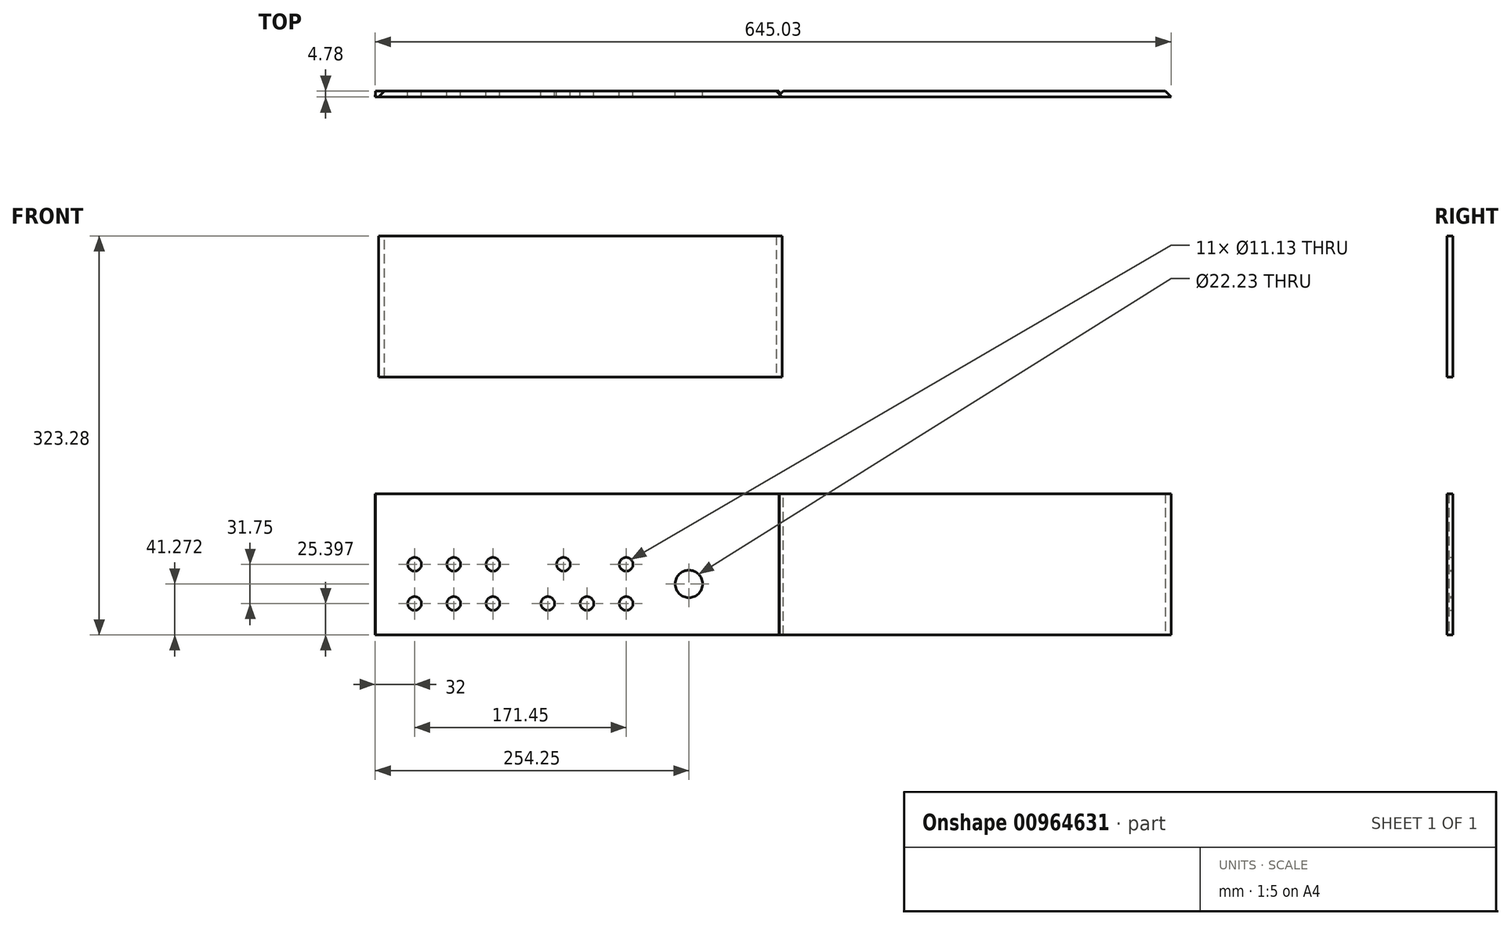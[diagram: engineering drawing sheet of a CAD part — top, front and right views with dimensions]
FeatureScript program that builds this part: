
annotation { "Feature Type Name" : "Feature", "Feature Type Description" : "" }
export const myFeature = defineFeature(function(context is Context, id is Id, definition is map)
    precondition{}
    {
        {
            var Q0;
            Q0=qCreatedBy(makeId("Front.planeOp"),FACE);
            var sketch = newSketch(context, id + "F0", { "sketchPlane" : qUnion([Q0])});
            skLineSegment(sketch, "E0.bottom", {"start": v(-189.37, 59.29) * mm, "end": v(137.66, 59.29) * mm});
            skLineSegment(sketch, "E0.top", {"start": v(-189.37, -55.01) * mm, "end": v(137.66, -55.01) * mm});
            skLineSegment(sketch, "E0.left", {"start": v(-189.37, 59.29) * mm, "end": v(-189.37, -55.01) * mm});
            skLineSegment(sketch, "E0.right", {"start": v(137.66, 59.29) * mm, "end": v(137.66, -55.01) * mm});
            skLineSegment(sketch, "E1.bottom", {"start": v(137.9, 59.29) * mm, "end": v(455.4, 59.29) * mm});
            skLineSegment(sketch, "E1.top", {"start": v(137.9, -55.01) * mm, "end": v(455.4, -55.01) * mm});
            skLineSegment(sketch, "E1.left", {"start": v(137.9, 59.29) * mm, "end": v(137.9, -55.01) * mm});
            skLineSegment(sketch, "E1.right", {"start": v(455.4, 59.29) * mm, "end": v(455.4, -55.01) * mm});
            skLineSegment(sketch, "E2.left", {"start": v(-189.62, 59.29) * mm, "end": v(-189.62, -55.01) * mm});
            skCircle(sketch, "E3", {"center": v(-157.62, -29.61) * mm, "radius": 5.56 * mm});
            skCircle(sketch, "E4", {"center": v(-125.87, -29.61) * mm, "radius": 5.56 * mm});
            skCircle(sketch, "E5", {"center": v(-94.12, -29.61) * mm, "radius": 5.56 * mm});
            skCircle(sketch, "E6", {"center": v(-17.92, -29.61) * mm, "radius": 5.56 * mm});
            skCircle(sketch, "E7", {"center": v(-49.67, -29.61) * mm, "radius": 5.56 * mm});
            skCircle(sketch, "E8", {"center": v(13.83, -29.61) * mm, "radius": 5.56 * mm});
            skCircle(sketch, "E9", {"center": v(-157.62, 2.14) * mm, "radius": 5.56 * mm});
            skCircle(sketch, "E10", {"center": v(-125.87, 2.14) * mm, "radius": 5.56 * mm});
            skCircle(sketch, "E11", {"center": v(-94.12, 2.14) * mm, "radius": 5.56 * mm});
            skCircle(sketch, "E12", {"center": v(-36.97, 2.14) * mm, "radius": 5.56 * mm});
            skCircle(sketch, "E13", {"center": v(13.83, 2.14) * mm, "radius": 5.56 * mm});
            skPoint(sketch, "E14", {"position": v(-157.62, -3.51) * mm});
            skCircle(sketch, "E15", {"center": v(64.63, -13.74) * mm, "radius": 11.11 * mm});
            skLineSegment(sketch, "E16", {"start": v(30.11, 2.14) * mm, "end": v(-174.63, 2.14) * mm, "construction": true});
            skLineSegment(sketch, "E17", {"start": v(-175, -29.61) * mm, "end": v(32.3, -29.61) * mm, "construction": true});
            skLineSegment(sketch, "E18", {"start": v(35.92, -13.74) * mm, "end": v(93.64, -13.74) * mm, "construction": true});
            skLineSegment(sketch, "E19.bottom", {"start": v(137.66, 59.29) * mm, "end": v(137.9, 59.29) * mm});
            skLineSegment(sketch, "E19.top", {"start": v(137.66, -55.01) * mm, "end": v(137.9, -55.01) * mm});
            skLineSegment(sketch, "E20.bottom", {"start": v(-189.62, 59.29) * mm, "end": v(-189.37, 59.29) * mm});
            skLineSegment(sketch, "E20.top", {"start": v(-189.62, -55.01) * mm, "end": v(-189.37, -55.01) * mm});
            skLineSegment(sketch, "E21.bottom", {"start": v(-186.96, 268.27) * mm, "end": v(140.07, 268.27) * mm});
            skLineSegment(sketch, "E21.top", {"start": v(-186.96, 153.97) * mm, "end": v(140.07, 153.97) * mm});
            skLineSegment(sketch, "E21.left", {"start": v(-186.96, 268.27) * mm, "end": v(-186.96, 153.97) * mm});
            skLineSegment(sketch, "E21.right", {"start": v(140.07, 268.27) * mm, "end": v(140.07, 153.97) * mm});
            skLineSegment(sketch, "E22.bottom", {"start": v(-507.12, 59.29) * mm, "end": v(-189.62, 59.29) * mm});
            skLineSegment(sketch, "E22.top", {"start": v(-507.12, -55.01) * mm, "end": v(-189.62, -55.01) * mm});
            skLineSegment(sketch, "E22.left", {"start": v(-507.12, 59.29) * mm, "end": v(-507.12, -55.01) * mm});
            skSolve(sketch);
        }
        {
            var Q0;
            Q0=makeQuery(id+"F0.imprint","IMPRINT",FACE,{"disambiguationData":[TD([[makeQuery(id+"F0.imprint","IMPRINT",EDGE,{"derivedFrom":sQuery(id+"F0.wireOp",EDGE,"E2.bottom")}),1.0]])]});
            var Q1;
            Q1=makeQuery(id+"F0.imprint","IMPRINT",FACE,{"disambiguationData":[TD([[makeQuery(id+"F0.imprint","IMPRINT",EDGE,{"derivedFrom":sQuery(id+"F0.wireOp",EDGE,"E0.bottom")}),-1.0]])]});
            var Q2;
            Q2=makeQuery(id+"F0.imprint","IMPRINT",FACE,{"disambiguationData":[TD([[makeQuery(id+"F0.imprint","IMPRINT",EDGE,{"derivedFrom":sQuery(id+"F0.wireOp",EDGE,"E1.bottom")}),-1.0]])]});
            extrude(context, id + "F1", {"entities" : qUnion([Q0, Q1, Q2]), "depth" : 4.78 * mm, "offsetDistance" : 25.4 * mm});
        }
        {
            var Q0;
            Q0=makeQuery(id+"F0.imprint","IMPRINT",FACE,{"disambiguationData":[TD([[makeQuery(id+"F0.imprint","IMPRINT",EDGE,{"derivedFrom":sQuery(id+"F0.wireOp",EDGE,"E20.bottom")}),-1.0]])]});
            var Q1;
            Q1=makeQuery(id+"F0.imprint","IMPRINT",FACE,{"disambiguationData":[TD([[makeQuery(id+"F0.imprint","IMPRINT",EDGE,{"derivedFrom":sQuery(id+"F0.wireOp",EDGE,"E19.bottom")}),-1.0]])]});
            extrude(context, id + "F2", {"entities" : qUnion([Q0, Q1]), "depth" : 1.59 * mm, "offsetDistance" : 25.4 * mm});
        }
        {
            var Q0;
            Q0=makeQuery(id+"F1.opExtrude","CAP_EDGE",EDGE,{"disambiguationData":[OSD([sQuery(id+"F0.wireOp",EDGE,"E2.right")])],"isStart":true});
            var Q1;
            Q1=makeQuery(id+"F1.opExtrude","CAP_EDGE",EDGE,{"disambiguationData":[OSD([sQuery(id+"F0.wireOp",EDGE,"E1.right")])],"isStart":true});
            chamfer(context, id + "F3", {"entities" : qUnion([Q0, Q1]), "width" : 4.78 * mm, "tangentPropagation" : true});
        }
        {
            var Q0;
            Q0=makeQuery(id+"F2.opExtrude","SWEPT_BODY",BODY,{"disambiguationData":[OSD([sQuery(id+"F0.wireOp",EDGE,"E20.bottom"),sQuery(id+"F0.wireOp",EDGE,"E20.top"),sQuery(id+"F0.wireOp",EDGE,"E2.left"),sQuery(id+"F0.wireOp",EDGE,"E0.left")])]});
            var Q1;
            Q1=makeQuery(id+"F2.opExtrude","SWEPT_BODY",BODY,{"disambiguationData":[OSD([sQuery(id+"F0.wireOp",EDGE,"E19.bottom"),sQuery(id+"F0.wireOp",EDGE,"E19.top"),sQuery(id+"F0.wireOp",EDGE,"E0.right"),sQuery(id+"F0.wireOp",EDGE,"E1.left")])]});
            transform(context, id + "F4", {"entities" : qUnion([Q0, Q1]), "transformType" : TransformType.TRANSLATION_3D, "dx" : 0 * mm, "dy" : -3.17 * mm, "dz" : 0 * mm, "makeCopy" : false});
        }
        {
            var Q0;
            Q0=makeQuery(id+"F1.opExtrude","CAP_EDGE",EDGE,{"disambiguationData":[OSD([sQuery(id+"F0.wireOp",EDGE,"E2.left")])],"isStart":true});
            var Q1;
            Q1=makeQuery(id+"F1.opExtrude","CAP_EDGE",EDGE,{"disambiguationData":[OSD([sQuery(id+"F0.wireOp",EDGE,"E0.left")])],"isStart":true});
            var Q2;
            Q2=makeQuery(id+"F1.opExtrude","CAP_EDGE",EDGE,{"disambiguationData":[OSD([sQuery(id+"F0.wireOp",EDGE,"E0.right")])],"isStart":true});
            var Q3;
            Q3=makeQuery(id+"F1.opExtrude","CAP_EDGE",EDGE,{"disambiguationData":[OSD([sQuery(id+"F0.wireOp",EDGE,"E1.left")])],"isStart":true});
            chamfer(context, id + "F5", {"entities" : qUnion([Q0, Q1, Q2, Q3]), "width" : 3.17 * mm, "tangentPropagation" : true});
        }
        {
            var Q0;
            Q0=makeQuery(id+"F0.imprint","IMPRINT",FACE,{"disambiguationData":[TD([[makeQuery(id+"F0.imprint","IMPRINT",EDGE,{"derivedFrom":sQuery(id+"F0.wireOp",EDGE,"E21.bottom")}),-1.0]])]});
            extrude(context, id + "F6", {"entities" : qUnion([Q0]), "depth" : 4.78 * mm, "offsetDistance" : 25.4 * mm});
        }
        {
            var Q0;
            Q0=makeQuery(id+"F6.opExtrude","CAP_EDGE",EDGE,{"disambiguationData":[OSD([sQuery(id+"F0.wireOp",EDGE,"E21.left")])],"isStart":true});
            var Q1;
            Q1=makeQuery(id+"F6.opExtrude","CAP_EDGE",EDGE,{"disambiguationData":[OSD([sQuery(id+"F0.wireOp",EDGE,"E21.right")])],"isStart":true});
            chamfer(context, id + "F7", {"entities" : qUnion([Q0, Q1]), "width" : 4.78 * mm, "tangentPropagation" : true});
        }
    });
